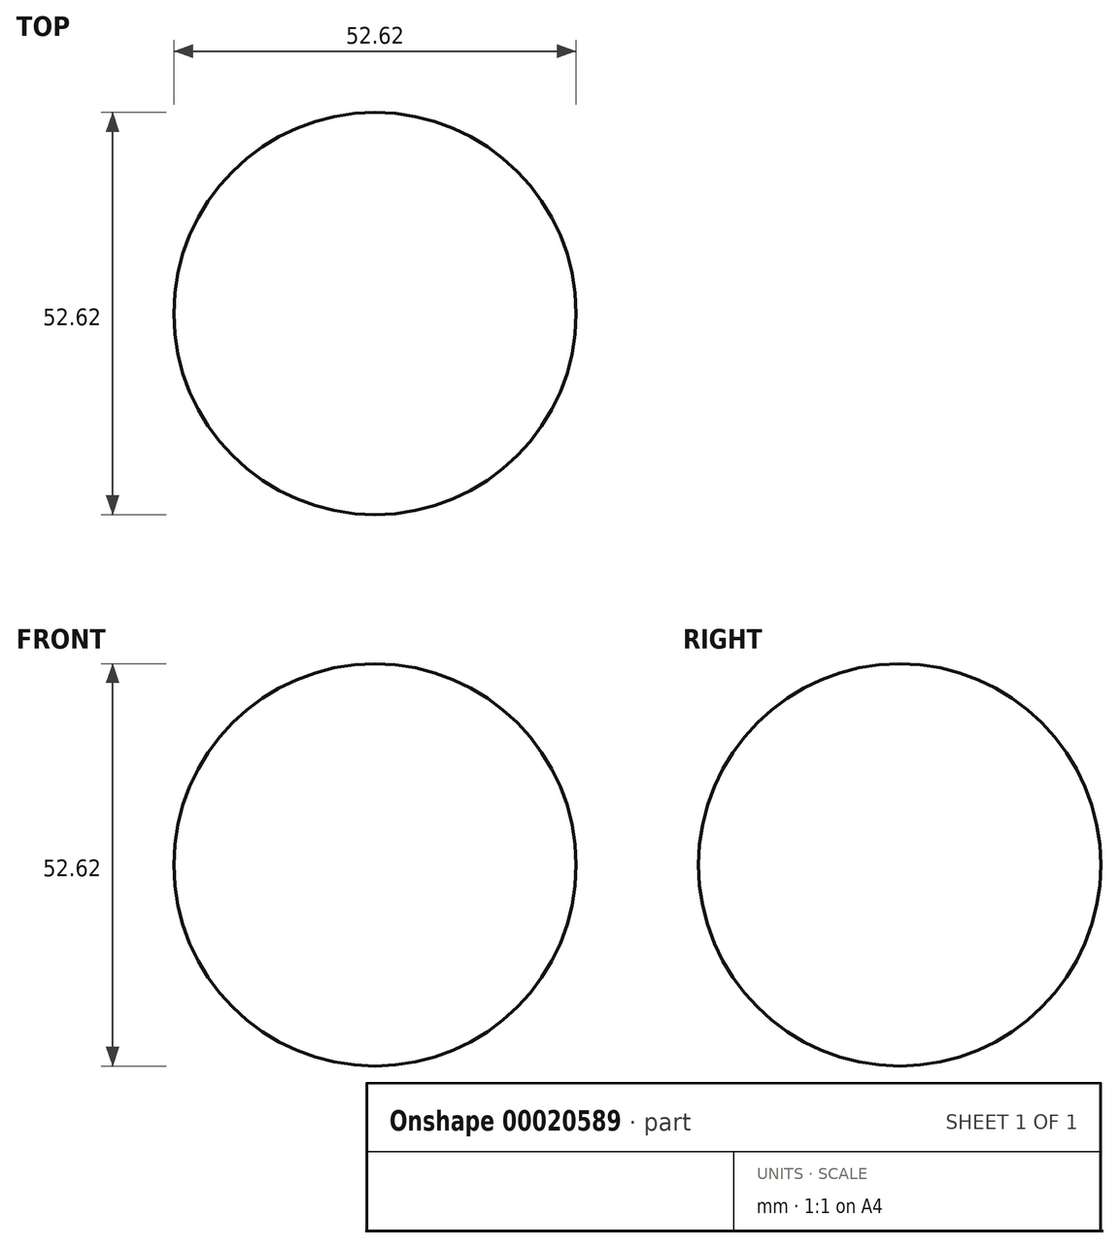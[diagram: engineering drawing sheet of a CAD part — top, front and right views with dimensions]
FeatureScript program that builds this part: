
annotation { "Feature Type Name" : "Feature", "Feature Type Description" : "" }
export const myFeature = defineFeature(function(context is Context, id is Id, definition is map)
    precondition{}
    {
        {
            var Q0;
            Q0=qCreatedBy(makeId("Top.planeOp"),FACE);
            var sketch = newSketch(context, id + "F0", { "sketchPlane" : qUnion([Q0])});
            skArc(sketch, "E0", {"start": v(0, -26.3) * mm, "mid": v(26.3, 0) * mm, "end": v(0, 26.3) * mm});
            skLineSegment(sketch, "E1", {"start": v(0, 0) * mm, "end": v(0, 34.64) * mm, "construction": true});
            skLineSegment(sketch, "E2", {"start": v(0, 26.3) * mm, "end": v(0, -26.3) * mm});
            skSolve(sketch);
        }
        {
            var Q0;
            Q0=makeQuery(id+"F0.imprint","IMPRINT",FACE,{"disambiguationData":[TD([[makeQuery(id+"F0.imprint","IMPRINT",EDGE,{"derivedFrom":sQuery(id+"F0.wireOp",EDGE,"E0")}),1.0]])]});
            var Q1;
            Q1=sQuery(id+"F0.wireOp",EDGE,"E1");
            revolve(context, id + "F1", {"entities" : qUnion([Q0]), "axis" : qUnion([Q1]), "revolveType" : RevolveType.FULL});
        }
    });
